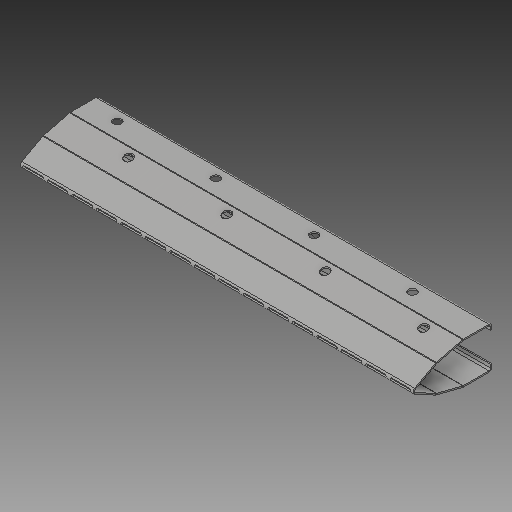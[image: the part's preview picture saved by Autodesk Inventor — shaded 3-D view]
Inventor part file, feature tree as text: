
AUTODESK INVENTOR PART (.ipt)
format: ipt  version: 2018 (Build 220112000, 112)  size: 820,224 bytes
history: native  units: mm
features: reference x25, other x23, sketch x14, sheet_metal_op x13, plane x9, projected_geometry x7, extrude x4
ambient origin geometry x8: Origin, YZ Plane, XZ Plane, XY Plane, X Axis, Y Axis, Z Axis, Center Point
bodies: Solid1 (feature_tree)
feature tree (95):
  plane  "Work Plane1"
  sheet_metal_op  "Face1"
  plane  "Work Plane2"
  sheet_metal_op  "Face2"
  plane  "Work Plane3"
  sheet_metal_op  "Face3"
  plane  "Work Plane4"
  sheet_metal_op  "Face4"
  plane  "Work Plane5"
  sheet_metal_op  "Face5"
  plane  "Work Plane6"
  sheet_metal_op  "Face6"
  plane  "Work Plane7"
  sheet_metal_op  "Face7"
  other  "midtplan"
  extrude  "Extrusion3"  Depth=5.0mm
  extrude  "hulsæt til stifter"  Depth=2.0mm
  plane  "Work Plane11"
  sketch  "Sketch13"  dims[d13=2.0mm]
  plane  "Work Plane12"
  extrude  "balusterhul"  Depth=5.0mm
  extrude  "balusterhul skråkompensering"  Depth=4.0mm
  sketch  "Sketch1"  dims[d0=4.0mm d1=5.0mm]
  reference  "Reference1"
  reference  "Reference2"
  reference  "Reference3"
  reference  "Reference4"
  other  "Plate1"
  sketch  "Sketch2"  dims[d2=4.0mm d3=2.0mm]
  reference  "Reference5"
  reference  "Reference6"
  reference  "Reference7"
  reference  "Reference8"
  other  "Plate2"
  sheet_metal_op  "Bend1"
  sketch  "Sketch3"  dims[d4=8.0mm d5=5.0mm]
  reference  "Reference9"
  reference  "Reference10"
  reference  "Reference11"
  other  "Plate3"
  sheet_metal_op  "Bend2"
  sketch  "Sketch4"  dims[d6=5.0mm d7=4.0mm]
  reference  "Reference12"
  reference  "Reference13"
  reference  "Reference14"
  reference  "Reference15"
  other  "Plate4"
  sheet_metal_op  "Bend3"
  sketch  "Sketch5"  dims[d8=2.0mm]
  reference  "Reference16"
  reference  "Reference17"
  reference  "Reference18"
  other  "Plate5"
  sheet_metal_op  "Bend4"
  sketch  "Sketch6"  dims[d9=8.0mm]
  reference  "Reference19"
  reference  "Reference20"
  reference  "Reference21"
  other  "Plate6"
  sheet_metal_op  "Bend5"
  sketch  "Sketch7"  dims[d10=5.0mm]
  reference  "Reference22"
  reference  "Reference23"
  other  "Plate7"
  sheet_metal_op  "Bend6"
  sketch  "Sketch8"  dims[d11=5.0mm]
  reference  "Reference24"
  projected_geometry  "Projected Loop1"
  other  "huller til stifter"
  projected_geometry  "Projected Loop3"
  sketch  "Sketch12"  dims[d12=4.0mm]
  projected_geometry  "Projected Loop4"
  reference  "Reference25"
  sketch  "Sketch14"  dims[d14=8.0mm]
  sketch  "Sketch15"  dims[d15=5.0mm]
  projected_geometry  "Projected Loop5"
  projected_geometry  "Projected Loop6"
  sketch  "Sketch16"  dims[d16=5.0mm]
  projected_geometry  "Projected Loop7"
  projected_geometry  "Projected Loop8"
  sketch  "Sketch17"  dims[d17=4.0mm d18=2.0mm d19=8.0mm d20=5.0mm d21=5.0mm d22=4.0mm d23=2.0mm d24=8.0mm d25=5.0mm d26=5.0mm d27=4.0mm d28=2.0mm d29=8.0mm d30=5.0mm d31=4.0mm d32=0.0mm d33=3.0mm d39=250.0mm d41=33.7mm d42=33.7mm d43=60.0mm d44=60.0mm d45=16.85mm d46=65.0mm d47=60.0mm d48=10.0mm d49=0.0mm d68=291.052mm d69=10.0mm d70=0.0mm d73=96.672mm d77=40.001254mm d78=26.6mm d79=25.8mm d80=40.0mm d82=302.737mm d83=10.0mm d85=10.0mm d87=302.737mm d88=113.655385mm d89=56.827692mm d90=90.0deg d91=90.0deg d92=49.5mm d93=100.0mm d94=0.0mm d97=2.728615mm d98=1.364307mm d99=10.0mm d100=0.0mm d101=90.0mm d102=30.0mm d103=521.995413mm d104=342.76471mm d106=342.76471mm d107=30.0mm d108=30.0mm d109=342.76471mm d110=30.0mm d111=342.76471mm d112=624.298717mm d113=10.0mm d114=4.0mm d115=0.0mm d116=221.534007mm d117=119.230703mm d118=96.672222mm d119=62.65387mm d120=1208.948mm d121=8.0mm d122=62.8mm d123=6.0mm d124=170.0mm d126=75.36mm d127=10.0mm d129=10.0mm d131=4.0mm d132=0.0mm d133=12.56mm]
  other  "Cut1"
  other  "plantehuller"
  other  "bukkeperforering"
  parser-record x4  (decoder bookkeeping rows leaked as tree rows — omitted from the tree; the rows remain in map.json)
  other  "modul.iam"
  other  "model:1"
  other  "Definition1"
  other  "søjle+vange.iam"
  other  "modul top:1"
  other  "plade top:1"
  other  "modul top.iam"
note: 4 file-system paths scrubbed to <path> (originals preserved in map.json)
